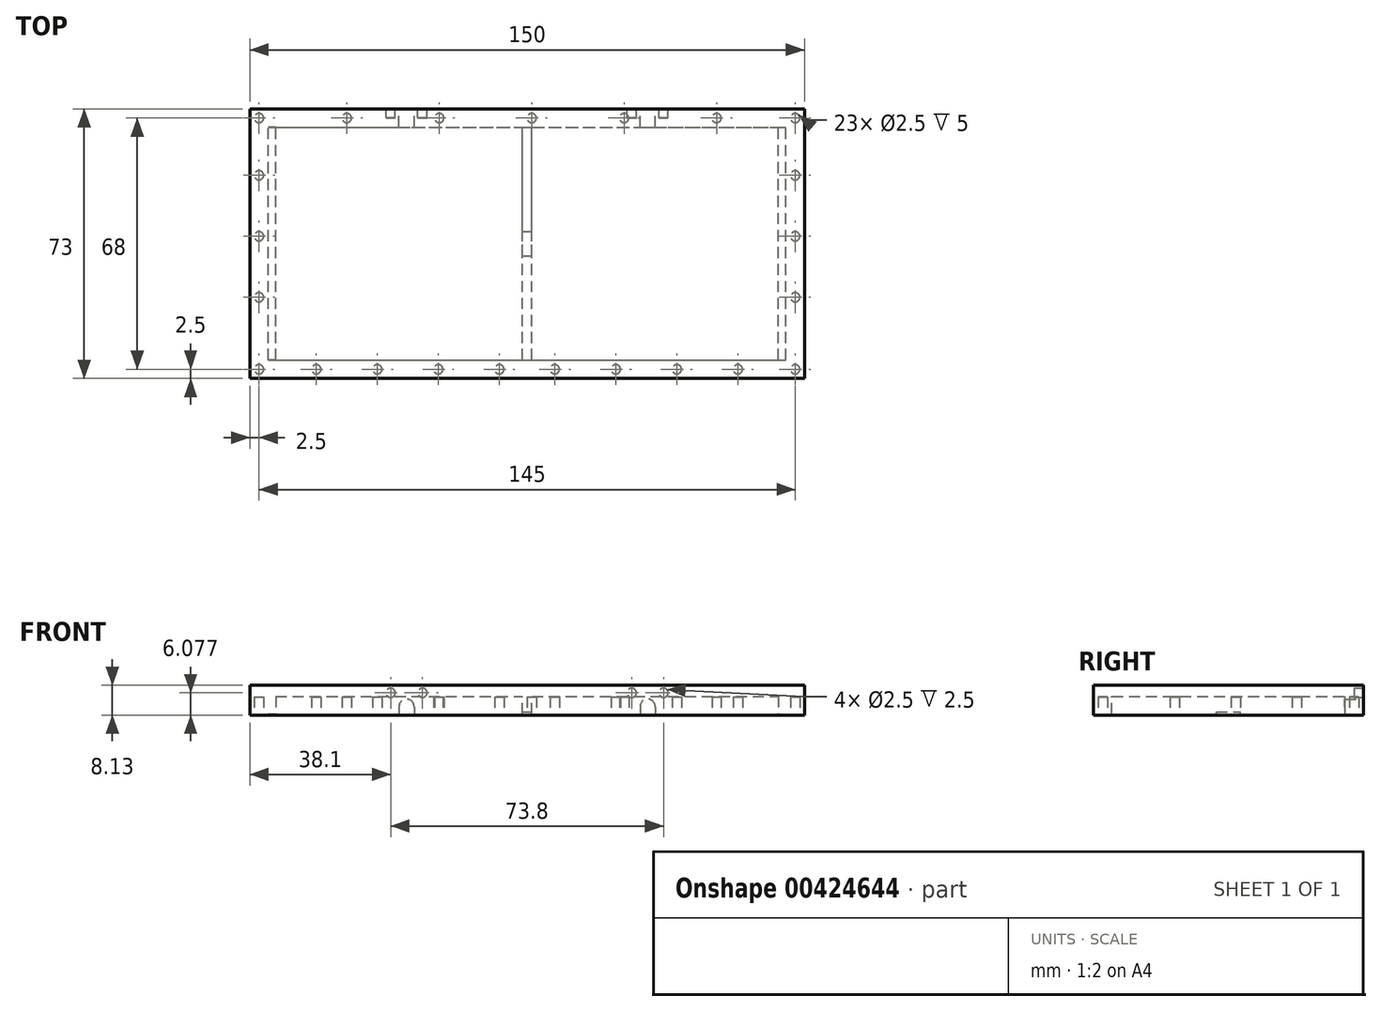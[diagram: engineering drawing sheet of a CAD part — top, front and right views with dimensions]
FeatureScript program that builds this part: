
annotation { "Feature Type Name" : "Feature", "Feature Type Description" : "" }
export const myFeature = defineFeature(function(context is Context, id is Id, definition is map)
    precondition{}
    {
        {
            var Q0;
            Q0=qCreatedBy(makeId("Top.planeOp"),FACE);
            var sketch = newSketch(context, id + "F0", { "sketchPlane" : qUnion([Q0])});
            skLineSegment(sketch, "E0.bottom", {"start": v(0, 0) * mm, "end": v(150, 0) * mm});
            skLineSegment(sketch, "E0.top", {"start": v(0, 73) * mm, "end": v(150, 73) * mm});
            skLineSegment(sketch, "E0.left", {"start": v(0, 0) * mm, "end": v(0, 73) * mm});
            skLineSegment(sketch, "E0.right", {"start": v(150, 0) * mm, "end": v(150, 73) * mm});
            skSolve(sketch);
        }
        {
            var Q0;
            Q0=qSketchRegion(id+"F0",true);
            extrude(context, id + "F1", {"entities" : qUnion([Q0]), "depth" : 8.13 * mm});
        }
        {
            var Q0;
            Q0=qCreatedBy(makeId("Top.planeOp"),FACE);
            var sketch = newSketch(context, id + "F2", { "sketchPlane" : qUnion([Q0])});
            skLineSegment(sketch, "E1.bottom", {"start": v(7, 5) * mm, "end": v(143, 5) * mm});
            skLineSegment(sketch, "E1.top", {"start": v(7, 68) * mm, "end": v(143, 68) * mm});
            skLineSegment(sketch, "E1.left", {"start": v(7, 5) * mm, "end": v(7, 68) * mm});
            skLineSegment(sketch, "E1.right", {"start": v(143, 5) * mm, "end": v(143, 68) * mm});
            skSolve(sketch);
        }
        {
            var Q0;
            Q0=makeQuery(id+"FBTdZfje9oESd4h_1.boolean.opBoolean","MERGE",FACE,{"derivedFrom":[makeQuery(id+"F1.opExtrude","CAP_FACE",FACE,{"disambiguationData":[OSD([sQuery(id+"F0.wireOp",EDGE,"E0.bottom"),sQuery(id+"F0.wireOp",EDGE,"E0.top"),sQuery(id+"F0.wireOp",EDGE,"E0.left"),sQuery(id+"F0.wireOp",EDGE,"E0.right")])],"isStart":true}),makeQuery(id+"FBTdZfje9oESd4h_1.opExtrude","SWEPT_FACE",FACE,{"disambiguationData":[OSD([sQuery(id+"Fv8mD8NBVYPvEqm_1.wireOp",EDGE,"SW5fG8um-qWP8-ISq3-XbeF-8tmbcfxiggH7.bottom")])]})]});
            var sketch = newSketch(context, id + "F3", { "sketchPlane" : qUnion([Q0])});
            skCircle(sketch, "E2", {"center": v(2.5, -2.5) * mm, "radius": 1.25 * mm});
            skSolve(sketch);
        }
        {
            var Q0;
            Q0=qSketchRegion(id+"F3",true);
            extrude(context, id + "F4", {"entities" : qUnion([Q0]), "operationType" : NewBodyOperationType.REMOVE, "oppositeDirection" : true, "depth" : 5 * mm});
        }
        {
            var Q0;
            Q0=makeQuery(id+"FBTdZfje9oESd4h_1.boolean.opBoolean","MERGE",FACE,{"derivedFrom":[makeQuery(id+"F1.opExtrude","CAP_FACE",FACE,{"disambiguationData":[OSD([sQuery(id+"F0.wireOp",EDGE,"E0.bottom"),sQuery(id+"F0.wireOp",EDGE,"E0.top"),sQuery(id+"F0.wireOp",EDGE,"E0.left"),sQuery(id+"F0.wireOp",EDGE,"E0.right")])],"isStart":true}),makeQuery(id+"FBTdZfje9oESd4h_1.opExtrude","SWEPT_FACE",FACE,{"disambiguationData":[OSD([sQuery(id+"Fv8mD8NBVYPvEqm_1.wireOp",EDGE,"SW5fG8um-qWP8-ISq3-XbeF-8tmbcfxiggH7.bottom")])]})]});
            var sketch = newSketch(context, id + "F5", { "sketchPlane" : qUnion([Q0])});
            skCircle(sketch, "E3", {"center": v(2.5, -22) * mm, "radius": 1.25 * mm});
            skSolve(sketch);
        }
        {
            var Q0;
            Q0=qSketchRegion(id+"F5",true);
            extrude(context, id + "F6", {"entities" : qUnion([Q0]), "operationType" : NewBodyOperationType.REMOVE, "oppositeDirection" : true, "depth" : 5 * mm});
        }
        {
            var Q0;
            Q0=makeQuery(id+"FBTdZfje9oESd4h_1.boolean.opBoolean","MERGE",FACE,{"derivedFrom":[makeQuery(id+"F1.opExtrude","CAP_FACE",FACE,{"disambiguationData":[OSD([sQuery(id+"F0.wireOp",EDGE,"E0.bottom"),sQuery(id+"F0.wireOp",EDGE,"E0.top"),sQuery(id+"F0.wireOp",EDGE,"E0.left"),sQuery(id+"F0.wireOp",EDGE,"E0.right")])],"isStart":true}),makeQuery(id+"FBTdZfje9oESd4h_1.opExtrude","SWEPT_FACE",FACE,{"disambiguationData":[OSD([sQuery(id+"Fv8mD8NBVYPvEqm_1.wireOp",EDGE,"SW5fG8um-qWP8-ISq3-XbeF-8tmbcfxiggH7.bottom")])]})]});
            var sketch = newSketch(context, id + "F7", { "sketchPlane" : qUnion([Q0])});
            skCircle(sketch, "E4", {"center": v(147.5, -2.5) * mm, "radius": 1.25 * mm});
            skSolve(sketch);
        }
        {
            var Q0;
            Q0=qSketchRegion(id+"F7",true);
            extrude(context, id + "F8", {"entities" : qUnion([Q0]), "operationType" : NewBodyOperationType.REMOVE, "oppositeDirection" : true, "depth" : 5 * mm});
        }
        {
            var Q0;
            Q0=makeQuery(id+"FBTdZfje9oESd4h_1.boolean.opBoolean","MERGE",FACE,{"derivedFrom":[makeQuery(id+"F1.opExtrude","CAP_FACE",FACE,{"disambiguationData":[OSD([sQuery(id+"F0.wireOp",EDGE,"E0.bottom"),sQuery(id+"F0.wireOp",EDGE,"E0.top"),sQuery(id+"F0.wireOp",EDGE,"E0.left"),sQuery(id+"F0.wireOp",EDGE,"E0.right")])],"isStart":true}),makeQuery(id+"FBTdZfje9oESd4h_1.opExtrude","SWEPT_FACE",FACE,{"disambiguationData":[OSD([sQuery(id+"Fv8mD8NBVYPvEqm_1.wireOp",EDGE,"SW5fG8um-qWP8-ISq3-XbeF-8tmbcfxiggH7.bottom")])]})]});
            var sketch = newSketch(context, id + "F9", { "sketchPlane" : qUnion([Q0])});
            skCircle(sketch, "E5", {"center": v(147.5, -22) * mm, "radius": 1.25 * mm});
            skSolve(sketch);
        }
        {
            var Q0;
            Q0=qSketchRegion(id+"F9",true);
            extrude(context, id + "F10", {"entities" : qUnion([Q0]), "operationType" : NewBodyOperationType.REMOVE, "oppositeDirection" : true, "depth" : 5 * mm});
        }
        {
            var Q0;
            Q0=makeQuery(id+"FBTdZfje9oESd4h_1.boolean.opBoolean","MERGE",FACE,{"derivedFrom":[makeQuery(id+"F1.opExtrude","CAP_FACE",FACE,{"disambiguationData":[OSD([sQuery(id+"F0.wireOp",EDGE,"E0.bottom"),sQuery(id+"F0.wireOp",EDGE,"E0.top"),sQuery(id+"F0.wireOp",EDGE,"E0.left"),sQuery(id+"F0.wireOp",EDGE,"E0.right")])],"isStart":true}),makeQuery(id+"FBTdZfje9oESd4h_1.opExtrude","SWEPT_FACE",FACE,{"disambiguationData":[OSD([sQuery(id+"Fv8mD8NBVYPvEqm_1.wireOp",EDGE,"SW5fG8um-qWP8-ISq3-XbeF-8tmbcfxiggH7.bottom")])]})]});
            var sketch = newSketch(context, id + "F11", { "sketchPlane" : qUnion([Q0])});
            skCircle(sketch, "E6", {"center": v(2.5, -38.5) * mm, "radius": 1.25 * mm});
            skSolve(sketch);
        }
        {
            var Q0;
            Q0=qSketchRegion(id+"F11",true);
            extrude(context, id + "F12", {"entities" : qUnion([Q0]), "operationType" : NewBodyOperationType.REMOVE, "oppositeDirection" : true, "depth" : 5 * mm});
        }
        {
            var Q0;
            Q0=makeQuery(id+"FBTdZfje9oESd4h_1.boolean.opBoolean","MERGE",FACE,{"derivedFrom":[makeQuery(id+"F1.opExtrude","CAP_FACE",FACE,{"disambiguationData":[OSD([sQuery(id+"F0.wireOp",EDGE,"E0.bottom"),sQuery(id+"F0.wireOp",EDGE,"E0.top"),sQuery(id+"F0.wireOp",EDGE,"E0.left"),sQuery(id+"F0.wireOp",EDGE,"E0.right")])],"isStart":true}),makeQuery(id+"FBTdZfje9oESd4h_1.opExtrude","SWEPT_FACE",FACE,{"disambiguationData":[OSD([sQuery(id+"Fv8mD8NBVYPvEqm_1.wireOp",EDGE,"SW5fG8um-qWP8-ISq3-XbeF-8tmbcfxiggH7.bottom")])]})]});
            var sketch = newSketch(context, id + "F13", { "sketchPlane" : qUnion([Q0])});
            skCircle(sketch, "E7", {"center": v(147.5, -38.5) * mm, "radius": 1.25 * mm});
            skSolve(sketch);
        }
        {
            var Q0;
            Q0=qSketchRegion(id+"F13",true);
            extrude(context, id + "F14", {"entities" : qUnion([Q0]), "operationType" : NewBodyOperationType.REMOVE, "oppositeDirection" : true, "depth" : 5 * mm});
        }
        {
            var Q0;
            Q0=makeQuery(id+"FBTdZfje9oESd4h_1.boolean.opBoolean","MERGE",FACE,{"derivedFrom":[makeQuery(id+"F1.opExtrude","CAP_FACE",FACE,{"disambiguationData":[OSD([sQuery(id+"F0.wireOp",EDGE,"E0.bottom"),sQuery(id+"F0.wireOp",EDGE,"E0.top"),sQuery(id+"F0.wireOp",EDGE,"E0.left"),sQuery(id+"F0.wireOp",EDGE,"E0.right")])],"isStart":true}),makeQuery(id+"FBTdZfje9oESd4h_1.opExtrude","SWEPT_FACE",FACE,{"disambiguationData":[OSD([sQuery(id+"Fv8mD8NBVYPvEqm_1.wireOp",EDGE,"SW5fG8um-qWP8-ISq3-XbeF-8tmbcfxiggH7.bottom")])]})]});
            var sketch = newSketch(context, id + "F15", { "sketchPlane" : qUnion([Q0])});
            skCircle(sketch, "E8", {"center": v(2.5, -55) * mm, "radius": 1.25 * mm});
            skSolve(sketch);
        }
        {
            var Q0;
            Q0=qSketchRegion(id+"F15",true);
            extrude(context, id + "F16", {"entities" : qUnion([Q0]), "operationType" : NewBodyOperationType.REMOVE, "oppositeDirection" : true, "depth" : 5 * mm});
        }
        {
            var Q0;
            Q0=makeQuery(id+"FBTdZfje9oESd4h_1.boolean.opBoolean","MERGE",FACE,{"derivedFrom":[makeQuery(id+"F1.opExtrude","CAP_FACE",FACE,{"disambiguationData":[OSD([sQuery(id+"F0.wireOp",EDGE,"E0.bottom"),sQuery(id+"F0.wireOp",EDGE,"E0.top"),sQuery(id+"F0.wireOp",EDGE,"E0.left"),sQuery(id+"F0.wireOp",EDGE,"E0.right")])],"isStart":true}),makeQuery(id+"FBTdZfje9oESd4h_1.opExtrude","SWEPT_FACE",FACE,{"disambiguationData":[OSD([sQuery(id+"Fv8mD8NBVYPvEqm_1.wireOp",EDGE,"SW5fG8um-qWP8-ISq3-XbeF-8tmbcfxiggH7.bottom")])]})]});
            var sketch = newSketch(context, id + "F17", { "sketchPlane" : qUnion([Q0])});
            skCircle(sketch, "E9", {"center": v(147.5, -55) * mm, "radius": 1.25 * mm});
            skSolve(sketch);
        }
        {
            var Q0;
            Q0=qSketchRegion(id+"F17",true);
            extrude(context, id + "F18", {"entities" : qUnion([Q0]), "operationType" : NewBodyOperationType.REMOVE, "oppositeDirection" : true, "depth" : 5 * mm});
        }
        {
            var Q0;
            Q0=makeQuery(id+"FBTdZfje9oESd4h_1.boolean.opBoolean","MERGE",FACE,{"derivedFrom":[makeQuery(id+"F1.opExtrude","CAP_FACE",FACE,{"disambiguationData":[OSD([sQuery(id+"F0.wireOp",EDGE,"E0.bottom"),sQuery(id+"F0.wireOp",EDGE,"E0.top"),sQuery(id+"F0.wireOp",EDGE,"E0.left"),sQuery(id+"F0.wireOp",EDGE,"E0.right")])],"isStart":true}),makeQuery(id+"FBTdZfje9oESd4h_1.opExtrude","SWEPT_FACE",FACE,{"disambiguationData":[OSD([sQuery(id+"Fv8mD8NBVYPvEqm_1.wireOp",EDGE,"SW5fG8um-qWP8-ISq3-XbeF-8tmbcfxiggH7.bottom")])]})]});
            var sketch = newSketch(context, id + "F19", { "sketchPlane" : qUnion([Q0])});
            skCircle(sketch, "E10", {"center": v(2.5, -70.5) * mm, "radius": 1.25 * mm});
            skSolve(sketch);
        }
        {
            var Q0;
            Q0=qSketchRegion(id+"F19",true);
            extrude(context, id + "F20", {"entities" : qUnion([Q0]), "operationType" : NewBodyOperationType.REMOVE, "oppositeDirection" : true, "depth" : 5 * mm});
        }
        {
            var Q0;
            Q0=makeQuery(id+"FBTdZfje9oESd4h_1.boolean.opBoolean","MERGE",FACE,{"derivedFrom":[makeQuery(id+"F1.opExtrude","CAP_FACE",FACE,{"disambiguationData":[OSD([sQuery(id+"F0.wireOp",EDGE,"E0.bottom"),sQuery(id+"F0.wireOp",EDGE,"E0.top"),sQuery(id+"F0.wireOp",EDGE,"E0.left"),sQuery(id+"F0.wireOp",EDGE,"E0.right")])],"isStart":true}),makeQuery(id+"FBTdZfje9oESd4h_1.opExtrude","SWEPT_FACE",FACE,{"disambiguationData":[OSD([sQuery(id+"Fv8mD8NBVYPvEqm_1.wireOp",EDGE,"SW5fG8um-qWP8-ISq3-XbeF-8tmbcfxiggH7.bottom")])]})]});
            var sketch = newSketch(context, id + "F21", { "sketchPlane" : qUnion([Q0])});
            skCircle(sketch, "E11", {"center": v(147.5, -70.5) * mm, "radius": 1.25 * mm});
            skSolve(sketch);
        }
        {
            var Q0;
            Q0=qSketchRegion(id+"F21",true);
            extrude(context, id + "F22", {"entities" : qUnion([Q0]), "operationType" : NewBodyOperationType.REMOVE, "oppositeDirection" : true, "depth" : 5 * mm});
        }
        {
            var Q0;
            Q0=makeQuery(id+"FBTdZfje9oESd4h_1.boolean.opBoolean","MERGE",FACE,{"derivedFrom":[makeQuery(id+"F1.opExtrude","CAP_FACE",FACE,{"disambiguationData":[OSD([sQuery(id+"F0.wireOp",EDGE,"E0.bottom"),sQuery(id+"F0.wireOp",EDGE,"E0.top"),sQuery(id+"F0.wireOp",EDGE,"E0.left"),sQuery(id+"F0.wireOp",EDGE,"E0.right")])],"isStart":true}),makeQuery(id+"FBTdZfje9oESd4h_1.opExtrude","SWEPT_FACE",FACE,{"disambiguationData":[OSD([sQuery(id+"Fv8mD8NBVYPvEqm_1.wireOp",EDGE,"SW5fG8um-qWP8-ISq3-XbeF-8tmbcfxiggH7.bottom")])]})]});
            var sketch = newSketch(context, id + "F23", { "sketchPlane" : qUnion([Q0])});
            skCircle(sketch, "E12", {"center": v(18, -2.5) * mm, "radius": 1.25 * mm});
            skSolve(sketch);
        }
        {
            var Q0;
            Q0=qSketchRegion(id+"F23",true);
            extrude(context, id + "F24", {"entities" : qUnion([Q0]), "operationType" : NewBodyOperationType.REMOVE, "oppositeDirection" : true, "depth" : 5 * mm});
        }
        {
            var Q0;
            Q0=makeQuery(id+"FBTdZfje9oESd4h_1.boolean.opBoolean","MERGE",FACE,{"derivedFrom":[makeQuery(id+"F1.opExtrude","CAP_FACE",FACE,{"disambiguationData":[OSD([sQuery(id+"F0.wireOp",EDGE,"E0.bottom"),sQuery(id+"F0.wireOp",EDGE,"E0.top"),sQuery(id+"F0.wireOp",EDGE,"E0.left"),sQuery(id+"F0.wireOp",EDGE,"E0.right")])],"isStart":true}),makeQuery(id+"FBTdZfje9oESd4h_1.opExtrude","SWEPT_FACE",FACE,{"disambiguationData":[OSD([sQuery(id+"Fv8mD8NBVYPvEqm_1.wireOp",EDGE,"SW5fG8um-qWP8-ISq3-XbeF-8tmbcfxiggH7.bottom")])]})]});
            var sketch = newSketch(context, id + "F25", { "sketchPlane" : qUnion([Q0])});
            skCircle(sketch, "E13", {"center": v(26.25, -70.5) * mm, "radius": 1.25 * mm});
            skSolve(sketch);
        }
        {
            var Q0;
            Q0=qSketchRegion(id+"F25",true);
            extrude(context, id + "F26", {"entities" : qUnion([Q0]), "operationType" : NewBodyOperationType.REMOVE, "oppositeDirection" : true, "depth" : 5 * mm});
        }
        {
            var Q0;
            Q0=makeQuery(id+"FBTdZfje9oESd4h_1.boolean.opBoolean","MERGE",FACE,{"derivedFrom":[makeQuery(id+"F1.opExtrude","CAP_FACE",FACE,{"disambiguationData":[OSD([sQuery(id+"F0.wireOp",EDGE,"E0.bottom"),sQuery(id+"F0.wireOp",EDGE,"E0.top"),sQuery(id+"F0.wireOp",EDGE,"E0.left"),sQuery(id+"F0.wireOp",EDGE,"E0.right")])],"isStart":true}),makeQuery(id+"FBTdZfje9oESd4h_1.opExtrude","SWEPT_FACE",FACE,{"disambiguationData":[OSD([sQuery(id+"Fv8mD8NBVYPvEqm_1.wireOp",EDGE,"SW5fG8um-qWP8-ISq3-XbeF-8tmbcfxiggH7.bottom")])]})]});
            var sketch = newSketch(context, id + "F27", { "sketchPlane" : qUnion([Q0])});
            skCircle(sketch, "E14", {"center": v(34.5, -2.5) * mm, "radius": 1.25 * mm});
            skSolve(sketch);
        }
        {
            var Q0;
            Q0=qSketchRegion(id+"F27",true);
            extrude(context, id + "F28", {"entities" : qUnion([Q0]), "operationType" : NewBodyOperationType.REMOVE, "oppositeDirection" : true, "depth" : 5 * mm});
        }
        {
            var Q0;
            Q0=makeQuery(id+"FBTdZfje9oESd4h_1.boolean.opBoolean","MERGE",FACE,{"derivedFrom":[makeQuery(id+"F1.opExtrude","CAP_FACE",FACE,{"disambiguationData":[OSD([sQuery(id+"F0.wireOp",EDGE,"E0.bottom"),sQuery(id+"F0.wireOp",EDGE,"E0.top"),sQuery(id+"F0.wireOp",EDGE,"E0.left"),sQuery(id+"F0.wireOp",EDGE,"E0.right")])],"isStart":true}),makeQuery(id+"FBTdZfje9oESd4h_1.opExtrude","SWEPT_FACE",FACE,{"disambiguationData":[OSD([sQuery(id+"Fv8mD8NBVYPvEqm_1.wireOp",EDGE,"SW5fG8um-qWP8-ISq3-XbeF-8tmbcfxiggH7.bottom")])]})]});
            var sketch = newSketch(context, id + "F29", { "sketchPlane" : qUnion([Q0])});
            skCircle(sketch, "E15", {"center": v(51, -2.5) * mm, "radius": 1.25 * mm});
            skSolve(sketch);
        }
        {
            var Q0;
            Q0=qSketchRegion(id+"F29",true);
            extrude(context, id + "F30", {"entities" : qUnion([Q0]), "operationType" : NewBodyOperationType.REMOVE, "oppositeDirection" : true, "depth" : 5 * mm});
        }
        {
            var Q0;
            Q0=makeQuery(id+"FBTdZfje9oESd4h_1.boolean.opBoolean","MERGE",FACE,{"derivedFrom":[makeQuery(id+"F1.opExtrude","CAP_FACE",FACE,{"disambiguationData":[OSD([sQuery(id+"F0.wireOp",EDGE,"E0.bottom"),sQuery(id+"F0.wireOp",EDGE,"E0.top"),sQuery(id+"F0.wireOp",EDGE,"E0.left"),sQuery(id+"F0.wireOp",EDGE,"E0.right")])],"isStart":true}),makeQuery(id+"FBTdZfje9oESd4h_1.opExtrude","SWEPT_FACE",FACE,{"disambiguationData":[OSD([sQuery(id+"Fv8mD8NBVYPvEqm_1.wireOp",EDGE,"SW5fG8um-qWP8-ISq3-XbeF-8tmbcfxiggH7.bottom")])]})]});
            var sketch = newSketch(context, id + "F31", { "sketchPlane" : qUnion([Q0])});
            skCircle(sketch, "E16", {"center": v(51.25, -70.5) * mm, "radius": 1.25 * mm});
            skSolve(sketch);
        }
        {
            var Q0;
            Q0=qSketchRegion(id+"F31",true);
            extrude(context, id + "F32", {"entities" : qUnion([Q0]), "operationType" : NewBodyOperationType.REMOVE, "oppositeDirection" : true, "depth" : 5 * mm});
        }
        {
            var Q0;
            Q0=makeQuery(id+"FBTdZfje9oESd4h_1.boolean.opBoolean","MERGE",FACE,{"derivedFrom":[makeQuery(id+"F1.opExtrude","CAP_FACE",FACE,{"disambiguationData":[OSD([sQuery(id+"F0.wireOp",EDGE,"E0.bottom"),sQuery(id+"F0.wireOp",EDGE,"E0.top"),sQuery(id+"F0.wireOp",EDGE,"E0.left"),sQuery(id+"F0.wireOp",EDGE,"E0.right")])],"isStart":true}),makeQuery(id+"FBTdZfje9oESd4h_1.opExtrude","SWEPT_FACE",FACE,{"disambiguationData":[OSD([sQuery(id+"Fv8mD8NBVYPvEqm_1.wireOp",EDGE,"SW5fG8um-qWP8-ISq3-XbeF-8tmbcfxiggH7.bottom")])]})]});
            var sketch = newSketch(context, id + "F33", { "sketchPlane" : qUnion([Q0])});
            skCircle(sketch, "E17", {"center": v(67.5, -2.5) * mm, "radius": 1.25 * mm});
            skSolve(sketch);
        }
        {
            var Q0;
            Q0=qSketchRegion(id+"F33",true);
            extrude(context, id + "F34", {"entities" : qUnion([Q0]), "operationType" : NewBodyOperationType.REMOVE, "oppositeDirection" : true, "depth" : 5 * mm});
        }
        {
            var Q0;
            Q0=makeQuery(id+"FBTdZfje9oESd4h_1.boolean.opBoolean","MERGE",FACE,{"derivedFrom":[makeQuery(id+"F1.opExtrude","CAP_FACE",FACE,{"disambiguationData":[OSD([sQuery(id+"F0.wireOp",EDGE,"E0.bottom"),sQuery(id+"F0.wireOp",EDGE,"E0.top"),sQuery(id+"F0.wireOp",EDGE,"E0.left"),sQuery(id+"F0.wireOp",EDGE,"E0.right")])],"isStart":true}),makeQuery(id+"FBTdZfje9oESd4h_1.opExtrude","SWEPT_FACE",FACE,{"disambiguationData":[OSD([sQuery(id+"Fv8mD8NBVYPvEqm_1.wireOp",EDGE,"SW5fG8um-qWP8-ISq3-XbeF-8tmbcfxiggH7.bottom")])]})]});
            var sketch = newSketch(context, id + "F35", { "sketchPlane" : qUnion([Q0])});
            skCircle(sketch, "E18", {"center": v(76.25, -70.5) * mm, "radius": 1.25 * mm});
            skSolve(sketch);
        }
        {
            var Q0;
            Q0=qSketchRegion(id+"F35",true);
            extrude(context, id + "F36", {"entities" : qUnion([Q0]), "operationType" : NewBodyOperationType.REMOVE, "oppositeDirection" : true, "depth" : 5 * mm});
        }
        {
            var Q0;
            Q0=makeQuery(id+"FBTdZfje9oESd4h_1.boolean.opBoolean","MERGE",FACE,{"derivedFrom":[makeQuery(id+"F1.opExtrude","CAP_FACE",FACE,{"disambiguationData":[OSD([sQuery(id+"F0.wireOp",EDGE,"E0.bottom"),sQuery(id+"F0.wireOp",EDGE,"E0.top"),sQuery(id+"F0.wireOp",EDGE,"E0.left"),sQuery(id+"F0.wireOp",EDGE,"E0.right")])],"isStart":true}),makeQuery(id+"FBTdZfje9oESd4h_1.opExtrude","SWEPT_FACE",FACE,{"disambiguationData":[OSD([sQuery(id+"Fv8mD8NBVYPvEqm_1.wireOp",EDGE,"SW5fG8um-qWP8-ISq3-XbeF-8tmbcfxiggH7.bottom")])]})]});
            var sketch = newSketch(context, id + "F37", { "sketchPlane" : qUnion([Q0])});
            skCircle(sketch, "E19", {"center": v(82.5, -2.5) * mm, "radius": 1.25 * mm});
            skSolve(sketch);
        }
        {
            var Q0;
            Q0=qSketchRegion(id+"F37",true);
            extrude(context, id + "F38", {"entities" : qUnion([Q0]), "operationType" : NewBodyOperationType.REMOVE, "oppositeDirection" : true, "depth" : 5 * mm});
        }
        {
            var Q0;
            Q0=makeQuery(id+"FBTdZfje9oESd4h_1.boolean.opBoolean","MERGE",FACE,{"derivedFrom":[makeQuery(id+"F1.opExtrude","CAP_FACE",FACE,{"disambiguationData":[OSD([sQuery(id+"F0.wireOp",EDGE,"E0.bottom"),sQuery(id+"F0.wireOp",EDGE,"E0.top"),sQuery(id+"F0.wireOp",EDGE,"E0.left"),sQuery(id+"F0.wireOp",EDGE,"E0.right")])],"isStart":true}),makeQuery(id+"FBTdZfje9oESd4h_1.opExtrude","SWEPT_FACE",FACE,{"disambiguationData":[OSD([sQuery(id+"Fv8mD8NBVYPvEqm_1.wireOp",EDGE,"SW5fG8um-qWP8-ISq3-XbeF-8tmbcfxiggH7.bottom")])]})]});
            var sketch = newSketch(context, id + "F39", { "sketchPlane" : qUnion([Q0])});
            skCircle(sketch, "E20", {"center": v(99, -2.5) * mm, "radius": 1.25 * mm});
            skSolve(sketch);
        }
        {
            var Q0;
            Q0=qSketchRegion(id+"F39",true);
            extrude(context, id + "F40", {"entities" : qUnion([Q0]), "operationType" : NewBodyOperationType.REMOVE, "oppositeDirection" : true, "depth" : 5 * mm});
        }
        {
            var Q0;
            Q0=makeQuery(id+"FBTdZfje9oESd4h_1.boolean.opBoolean","MERGE",FACE,{"derivedFrom":[makeQuery(id+"F1.opExtrude","CAP_FACE",FACE,{"disambiguationData":[OSD([sQuery(id+"F0.wireOp",EDGE,"E0.bottom"),sQuery(id+"F0.wireOp",EDGE,"E0.top"),sQuery(id+"F0.wireOp",EDGE,"E0.left"),sQuery(id+"F0.wireOp",EDGE,"E0.right")])],"isStart":true}),makeQuery(id+"FBTdZfje9oESd4h_1.opExtrude","SWEPT_FACE",FACE,{"disambiguationData":[OSD([sQuery(id+"Fv8mD8NBVYPvEqm_1.wireOp",EDGE,"SW5fG8um-qWP8-ISq3-XbeF-8tmbcfxiggH7.bottom")])]})]});
            var sketch = newSketch(context, id + "F41", { "sketchPlane" : qUnion([Q0])});
            skCircle(sketch, "E21", {"center": v(101.25, -70.5) * mm, "radius": 1.25 * mm});
            skSolve(sketch);
        }
        {
            var Q0;
            Q0=qSketchRegion(id+"F41",true);
            extrude(context, id + "F42", {"entities" : qUnion([Q0]), "operationType" : NewBodyOperationType.REMOVE, "oppositeDirection" : true, "depth" : 5 * mm});
        }
        {
            var Q0;
            Q0=makeQuery(id+"FBTdZfje9oESd4h_1.boolean.opBoolean","MERGE",FACE,{"derivedFrom":[makeQuery(id+"F1.opExtrude","CAP_FACE",FACE,{"disambiguationData":[OSD([sQuery(id+"F0.wireOp",EDGE,"E0.bottom"),sQuery(id+"F0.wireOp",EDGE,"E0.top"),sQuery(id+"F0.wireOp",EDGE,"E0.left"),sQuery(id+"F0.wireOp",EDGE,"E0.right")])],"isStart":true}),makeQuery(id+"FBTdZfje9oESd4h_1.opExtrude","SWEPT_FACE",FACE,{"disambiguationData":[OSD([sQuery(id+"Fv8mD8NBVYPvEqm_1.wireOp",EDGE,"SW5fG8um-qWP8-ISq3-XbeF-8tmbcfxiggH7.bottom")])]})]});
            var sketch = newSketch(context, id + "F43", { "sketchPlane" : qUnion([Q0])});
            skCircle(sketch, "E22", {"center": v(115.5, -2.5) * mm, "radius": 1.25 * mm});
            skSolve(sketch);
        }
        {
            var Q0;
            Q0=qSketchRegion(id+"F43",true);
            extrude(context, id + "F44", {"entities" : qUnion([Q0]), "operationType" : NewBodyOperationType.REMOVE, "oppositeDirection" : true, "depth" : 5 * mm});
        }
        {
            var Q0;
            Q0=makeQuery(id+"FBTdZfje9oESd4h_1.boolean.opBoolean","MERGE",FACE,{"derivedFrom":[makeQuery(id+"F1.opExtrude","CAP_FACE",FACE,{"disambiguationData":[OSD([sQuery(id+"F0.wireOp",EDGE,"E0.bottom"),sQuery(id+"F0.wireOp",EDGE,"E0.top"),sQuery(id+"F0.wireOp",EDGE,"E0.left"),sQuery(id+"F0.wireOp",EDGE,"E0.right")])],"isStart":true}),makeQuery(id+"FBTdZfje9oESd4h_1.opExtrude","SWEPT_FACE",FACE,{"disambiguationData":[OSD([sQuery(id+"Fv8mD8NBVYPvEqm_1.wireOp",EDGE,"SW5fG8um-qWP8-ISq3-XbeF-8tmbcfxiggH7.bottom")])]})]});
            var sketch = newSketch(context, id + "F45", { "sketchPlane" : qUnion([Q0])});
            skCircle(sketch, "E23", {"center": v(126.25, -70.5) * mm, "radius": 1.25 * mm});
            skSolve(sketch);
        }
        {
            var Q0;
            Q0=qSketchRegion(id+"F45",true);
            extrude(context, id + "F46", {"entities" : qUnion([Q0]), "operationType" : NewBodyOperationType.REMOVE, "oppositeDirection" : true, "depth" : 5 * mm});
        }
        {
            var Q0;
            Q0=makeQuery(id+"FBTdZfje9oESd4h_1.boolean.opBoolean","MERGE",FACE,{"derivedFrom":[makeQuery(id+"F1.opExtrude","CAP_FACE",FACE,{"disambiguationData":[OSD([sQuery(id+"F0.wireOp",EDGE,"E0.bottom"),sQuery(id+"F0.wireOp",EDGE,"E0.top"),sQuery(id+"F0.wireOp",EDGE,"E0.left"),sQuery(id+"F0.wireOp",EDGE,"E0.right")])],"isStart":true}),makeQuery(id+"FBTdZfje9oESd4h_1.opExtrude","SWEPT_FACE",FACE,{"disambiguationData":[OSD([sQuery(id+"Fv8mD8NBVYPvEqm_1.wireOp",EDGE,"SW5fG8um-qWP8-ISq3-XbeF-8tmbcfxiggH7.bottom")])]})]});
            var sketch = newSketch(context, id + "F47", { "sketchPlane" : qUnion([Q0])});
            skCircle(sketch, "E24", {"center": v(132, -2.5) * mm, "radius": 1.25 * mm});
            skSolve(sketch);
        }
        {
            var Q0;
            Q0=qSketchRegion(id+"F47",true);
            extrude(context, id + "F48", {"entities" : qUnion([Q0]), "operationType" : NewBodyOperationType.REMOVE, "oppositeDirection" : true, "depth" : 5 * mm});
        }
        {
            var Q0;
            Q0=qSketchRegion(id+"F2",true);
            extrude(context, id + "F49", {"entities" : qUnion([Q0]), "operationType" : NewBodyOperationType.REMOVE, "depth" : 5.13 * mm});
        }
        {
            var Q0;
            Q0=makeQuery(id+"F49.boolean.opBoolean","COPY",FACE,{"derivedFrom":makeQuery(id+"F49.opExtrude","CAP_FACE",FACE,{"disambiguationData":[OSD([sQuery(id+"F2.wireOp",EDGE,"E1.bottom"),sQuery(id+"F2.wireOp",EDGE,"E1.top"),sQuery(id+"F2.wireOp",EDGE,"E1.left"),sQuery(id+"F2.wireOp",EDGE,"E1.right")])],"isStart":false})});
            var sketch = newSketch(context, id + "F50", { "sketchPlane" : qUnion([Q0])});
            skLineSegment(sketch, "E25.bottom", {"start": v(73.75, -5) * mm, "end": v(76.25, -5) * mm});
            skLineSegment(sketch, "E25.top", {"start": v(73.75, -68) * mm, "end": v(76.25, -68) * mm});
            skLineSegment(sketch, "E25.left", {"start": v(73.75, -5) * mm, "end": v(73.75, -68) * mm});
            skLineSegment(sketch, "E25.right", {"start": v(76.25, -5) * mm, "end": v(76.25, -68) * mm});
            skSolve(sketch);
        }
        {
            var Q0;
            Q0=qSketchRegion(id+"F50",true);
            extrude(context, id + "F51", {"entities" : qUnion([Q0]), "operationType" : NewBodyOperationType.ADD, "depth" : 4.87 * mm});
        }
        {
            var Q0;
            Q0=makeQuery(id+"F51.opExtrude","SWEPT_FACE",FACE,{"disambiguationData":[OSD([sQuery(id+"F50.wireOp",EDGE,"E25.right")])]});
            var sketch = newSketch(context, id + "F52", { "sketchPlane" : qUnion([Q0])});
            skLineSegment(sketch, "E26.bottom", {"start": v(33.25, 0.25) * mm, "end": v(39.75, 0.25) * mm});
            skLineSegment(sketch, "E26.top", {"start": v(33.25, 0.88) * mm, "end": v(39.75, 0.88) * mm});
            skLineSegment(sketch, "E26.left", {"start": v(33.25, 0.25) * mm, "end": v(33.25, 0.88) * mm});
            skLineSegment(sketch, "E26.right", {"start": v(39.75, 0.25) * mm, "end": v(39.75, 0.88) * mm});
            skSolve(sketch);
        }
        {
            var Q0;
            Q0=qSketchRegion(id+"F52",true);
            extrude(context, id + "F53", {"entities" : qUnion([Q0]), "operationType" : NewBodyOperationType.REMOVE, "oppositeDirection" : true, "depth" : 2.5 * mm});
        }
        {
            var Q0;
            Q0=makeQuery(id+"F1.opExtrude","CAP_FACE",FACE,{"disambiguationData":[OSD([sQuery(id+"F0.wireOp",EDGE,"E0.bottom"),sQuery(id+"F0.wireOp",EDGE,"E0.top"),sQuery(id+"F0.wireOp",EDGE,"E0.left"),sQuery(id+"F0.wireOp",EDGE,"E0.right")])],"isStart":true});
            var sketch = newSketch(context, id + "F54", { "sketchPlane" : qUnion([Q0])});
            skLineSegment(sketch, "E27.bottom", {"start": v(7, -5) * mm, "end": v(5, -5) * mm});
            skLineSegment(sketch, "E27.top", {"start": v(7, -68) * mm, "end": v(5, -68) * mm});
            skLineSegment(sketch, "E27.left", {"start": v(7, -5) * mm, "end": v(7, -68) * mm});
            skLineSegment(sketch, "E27.right", {"start": v(5, -5) * mm, "end": v(5, -68) * mm});
            skSolve(sketch);
        }
        {
            var Q0;
            Q0=qSketchRegion(id+"F54",true);
            extrude(context, id + "F55", {"entities" : qUnion([Q0]), "operationType" : NewBodyOperationType.REMOVE, "oppositeDirection" : true, "depth" : 0.25 * mm});
        }
        {
            var Q0;
            Q0=makeQuery(id+"F1.opExtrude","CAP_FACE",FACE,{"disambiguationData":[OSD([sQuery(id+"F0.wireOp",EDGE,"E0.bottom"),sQuery(id+"F0.wireOp",EDGE,"E0.top"),sQuery(id+"F0.wireOp",EDGE,"E0.left"),sQuery(id+"F0.wireOp",EDGE,"E0.right")])],"isStart":true});
            var sketch = newSketch(context, id + "F56", { "sketchPlane" : qUnion([Q0])});
            skLineSegment(sketch, "E28.bottom", {"start": v(143, -5) * mm, "end": v(145, -5) * mm});
            skLineSegment(sketch, "E28.top", {"start": v(143, -68) * mm, "end": v(145, -68) * mm});
            skLineSegment(sketch, "E28.left", {"start": v(143, -5) * mm, "end": v(143, -68) * mm});
            skLineSegment(sketch, "E28.right", {"start": v(145, -5) * mm, "end": v(145, -68) * mm});
            skSolve(sketch);
        }
        {
            var Q0;
            Q0=qSketchRegion(id+"F56",true);
            extrude(context, id + "F57", {"entities" : qUnion([Q0]), "operationType" : NewBodyOperationType.REMOVE, "oppositeDirection" : true, "depth" : 0.25 * mm});
        }
        {
            var Q0;
            Q0=makeQuery(id+"F1.opExtrude","SWEPT_FACE",FACE,{"disambiguationData":[OSD([sQuery(id+"F0.wireOp",EDGE,"E0.top")])]});
            var sketch = newSketch(context, id + "F58", { "sketchPlane" : qUnion([Q0])});
            skCircle(sketch, "E29", {"center": v(-42.4, 2.3) * mm, "radius": 2.05 * mm});
            skSolve(sketch);
        }
        {
            var Q0;
            Q0=qSketchRegion(id+"F58",true);
            extrude(context, id + "F59", {"entities" : qUnion([Q0]), "operationType" : NewBodyOperationType.REMOVE, "oppositeDirection" : true, "depth" : 5 * mm});
        }
        {
            var Q0;
            Q0=makeQuery(id+"F1.opExtrude","SWEPT_FACE",FACE,{"disambiguationData":[OSD([sQuery(id+"F0.wireOp",EDGE,"E0.top")])]});
            var sketch = newSketch(context, id + "F60", { "sketchPlane" : qUnion([Q0])});
            skCircle(sketch, "E30", {"center": v(-107.6, 2.3) * mm, "radius": 2.05 * mm});
            skSolve(sketch);
        }
        {
            var Q0;
            Q0=qSketchRegion(id+"F60",true);
            extrude(context, id + "F61", {"entities" : qUnion([Q0]), "operationType" : NewBodyOperationType.REMOVE, "oppositeDirection" : true, "depth" : 5 * mm});
        }
        {
            var Q0;
            Q0=makeQuery(id+"F1.opExtrude","SWEPT_FACE",FACE,{"disambiguationData":[OSD([sQuery(id+"F0.wireOp",EDGE,"E0.top")])]});
            var sketch = newSketch(context, id + "F62", { "sketchPlane" : qUnion([Q0])});
            skLineSegment(sketch, "E31.bottom", {"start": v(-109.65, 2.3) * mm, "end": v(-105.55, 2.3) * mm});
            skLineSegment(sketch, "E31.top", {"start": v(-109.65, 0) * mm, "end": v(-105.55, 0) * mm});
            skLineSegment(sketch, "E31.left", {"start": v(-109.65, 2.3) * mm, "end": v(-109.65, 0) * mm});
            skLineSegment(sketch, "E31.right", {"start": v(-105.55, 2.3) * mm, "end": v(-105.55, 0) * mm});
            skSolve(sketch);
        }
        {
            var Q0;
            Q0=qSketchRegion(id+"F62",true);
            extrude(context, id + "F63", {"entities" : qUnion([Q0]), "operationType" : NewBodyOperationType.REMOVE, "oppositeDirection" : true, "depth" : 5 * mm});
        }
        {
            var Q0;
            Q0=makeQuery(id+"F1.opExtrude","SWEPT_FACE",FACE,{"disambiguationData":[OSD([sQuery(id+"F0.wireOp",EDGE,"E0.top")])]});
            var sketch = newSketch(context, id + "F64", { "sketchPlane" : qUnion([Q0])});
            skLineSegment(sketch, "E32.bottom", {"start": v(-44.45, 2.3) * mm, "end": v(-40.35, 2.3) * mm});
            skLineSegment(sketch, "E32.top", {"start": v(-44.45, 0) * mm, "end": v(-40.35, 0) * mm});
            skLineSegment(sketch, "E32.left", {"start": v(-44.45, 2.3) * mm, "end": v(-44.45, 0) * mm});
            skLineSegment(sketch, "E32.right", {"start": v(-40.35, 2.3) * mm, "end": v(-40.35, 0) * mm});
            skSolve(sketch);
        }
        {
            var Q0;
            Q0=qSketchRegion(id+"F64",true);
            extrude(context, id + "F65", {"entities" : qUnion([Q0]), "operationType" : NewBodyOperationType.REMOVE, "oppositeDirection" : true, "depth" : 5 * mm});
        }
        {
            var Q0;
            Q0=makeQuery(id+"F1.opExtrude","SWEPT_FACE",FACE,{"disambiguationData":[OSD([sQuery(id+"F0.wireOp",EDGE,"E0.top")])]});
            var sketch = newSketch(context, id + "F66", { "sketchPlane" : qUnion([Q0])});
            skCircle(sketch, "E33", {"center": v(-38.1, 6.08) * mm, "radius": 1.25 * mm});
            skCircle(sketch, "E34", {"center": v(-46.7, 6.08) * mm, "radius": 1.25 * mm});
            skCircle(sketch, "E35", {"center": v(-111.9, 6.08) * mm, "radius": 1.25 * mm});
            skCircle(sketch, "E36", {"center": v(-103.3, 6.08) * mm, "radius": 1.25 * mm});
            skSolve(sketch);
        }
        {
            var Q0;
            Q0=qSketchRegion(id+"F66",true);
            extrude(context, id + "F67", {"entities" : qUnion([Q0]), "operationType" : NewBodyOperationType.REMOVE, "oppositeDirection" : true, "depth" : 2.5 * mm});
        }
    });
